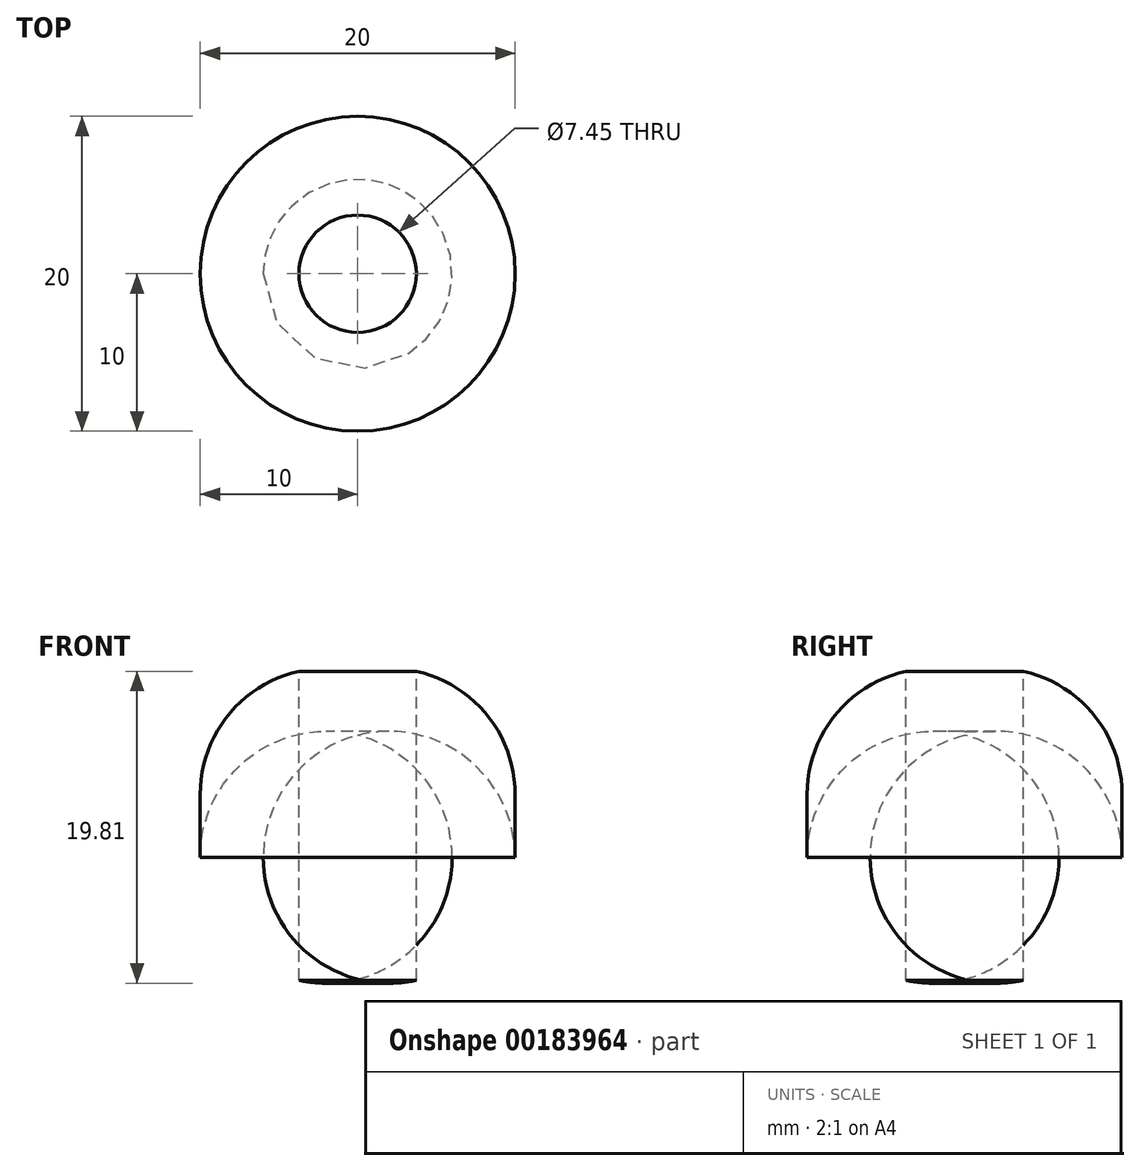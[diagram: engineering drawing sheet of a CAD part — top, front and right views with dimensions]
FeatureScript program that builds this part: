
annotation { "Feature Type Name" : "Feature", "Feature Type Description" : "" }
export const myFeature = defineFeature(function(context is Context, id is Id, definition is map)
    precondition{}
    {
        {
            var Q0;
            Q0=qCreatedBy(makeId("Top.planeOp"),FACE);
            var sketch = newSketch(context, id + "F0", { "sketchPlane" : qUnion([Q0])});
            skCircle(sketch, "E0", {"center": v(0, 0) * mm, "radius": 10 * mm});
            skSolve(sketch);
        }
        {
            var Q0;
            Q0=makeQuery(id+"F0.imprint","IMPRINT",FACE,{"disambiguationData":[TD([[makeQuery(id+"F0.imprint","IMPRINT",EDGE,{"derivedFrom":sQuery(id+"F0.wireOp",EDGE,"E0")}),1.0]])]});
            extrude(context, id + "F1", {"entities" : qUnion([Q0]), "depth" : 20 * mm});
        }
        {
            var Q0;
            Q0=makeQuery(id+"F1.opExtrude","CAP_FACE",FACE,{"disambiguationData":[OSD([sQuery(id+"F0.wireOp",EDGE,"E0")])],"isStart":false});
            var Q1;
            Q1=makeQuery(id+"F1.opExtrude","CAP_FACE",FACE,{"disambiguationData":[OSD([sQuery(id+"F0.wireOp",EDGE,"E0")])],"isStart":true});
            fillet(context, id + "F2", {"entities" : qUnion([Q0, Q1]), "radius" : 8 * mm, "tangentPropagation" : true, "allowEdgeOverflow" : false});
        }
        {
            var Q0;
            Q0=makeQuery(id+"F1.opExtrude","CAP_FACE",FACE,{"disambiguationData":[OSD([sQuery(id+"F0.wireOp",EDGE,"E0")])],"isStart":false});
            var sketch = newSketch(context, id + "F3", { "sketchPlane" : qUnion([Q0])});
            skCircle(sketch, "E1", {"center": v(0, 0) * mm, "radius": 3.73 * mm});
            skSolve(sketch);
        }
        {
            var Q0;
            {var subQ0=sQuery(id+"F0.wireOp",EDGE,"E0");Q0=makeQuery(id+"F3.imprint","IMPRINT",FACE,{"disambiguationData":[TD([[makeQuery(id+"F3.imprint","IMPRINT",EDGE,{"derivedFrom":makeQuery(id+"F2.opFillet","BLEND_EDGE",EDGE,{"blendedFrom":[makeQuery(id+"F1.opExtrude","CAP_EDGE",EDGE,{"disambiguationData":[OSD([subQ0])],"isStart":false}),makeQuery(id+"F1.opExtrude","CAP_FACE",FACE,{"disambiguationData":[OSD([subQ0])],"isStart":false})],"blendedInto":[makeQuery(id+"F1.opExtrude","CAP_FACE",FACE,{"disambiguationData":[OSD([subQ0])],"isStart":false})]})}),1.0]])]});}
            var Q1;
            Q1=makeQuery(id+"F3.imprint","IMPRINT",FACE,{"disambiguationData":[TD([[makeQuery(id+"F3.imprint","IMPRINT",EDGE,{"derivedFrom":sQuery(id+"F3.wireOp",EDGE,"E1")}),1.0]])]});
            extrude(context, id + "F4", {"entities" : qUnion([Q0, Q1]), "operationType" : NewBodyOperationType.REMOVE, "oppositeDirection" : true, "depth" : 20.1 * mm});
        }
    });
